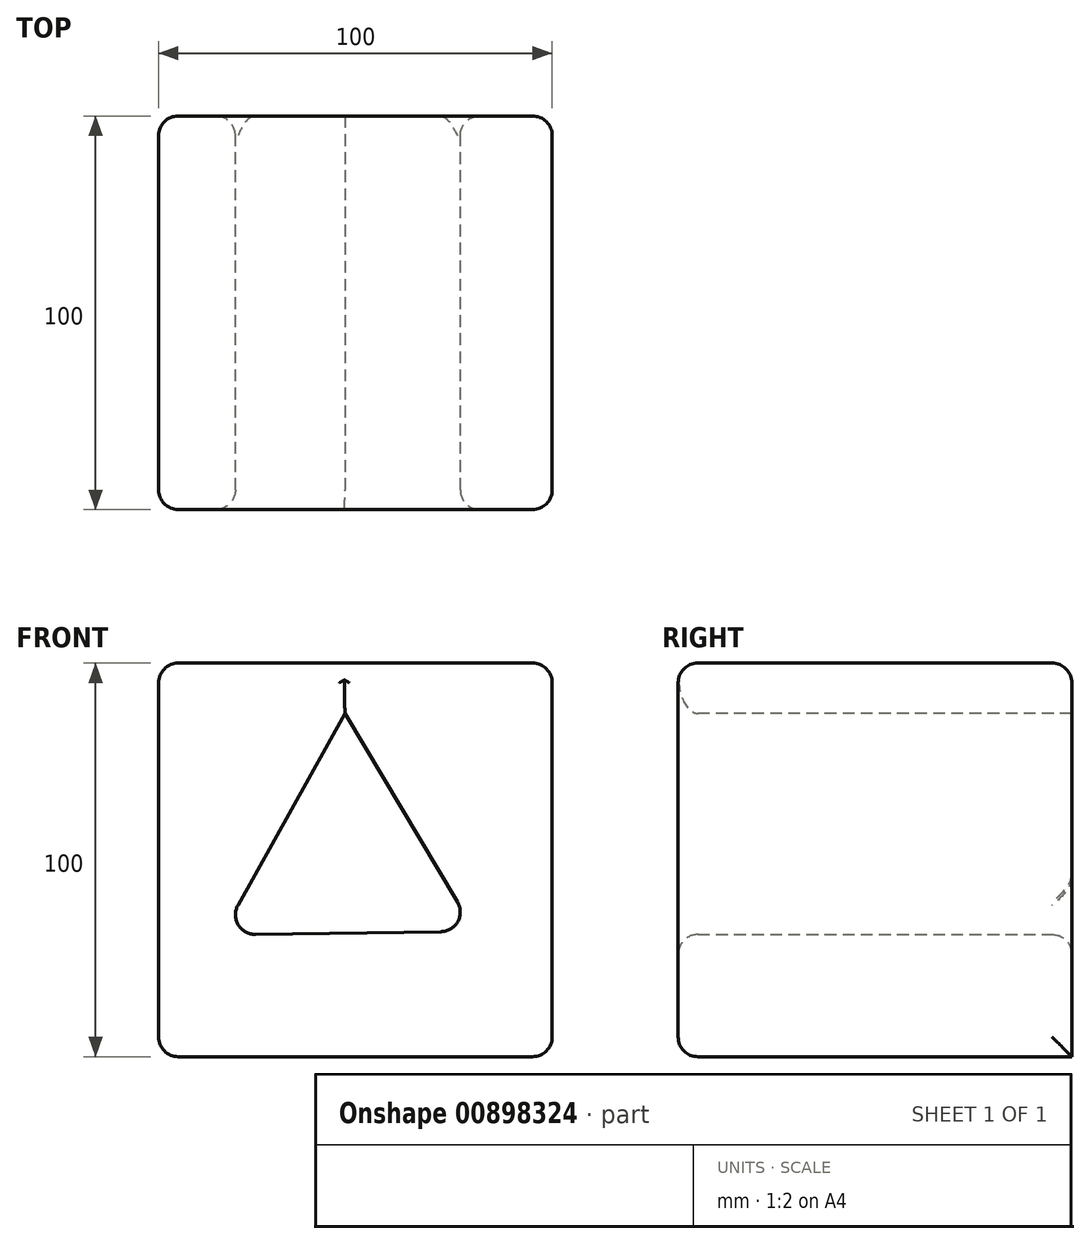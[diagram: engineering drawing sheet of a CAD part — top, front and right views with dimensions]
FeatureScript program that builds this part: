
annotation { "Feature Type Name" : "Feature", "Feature Type Description" : "" }
export const myFeature = defineFeature(function(context is Context, id is Id, definition is map)
    precondition{}
    {
        {
            var Q0;
            Q0=qCreatedBy(makeId("Front.planeOp"),FACE);
            var sketch = newSketch(context, id + "F0", { "sketchPlane" : qUnion([Q0])});
            skLineSegment(sketch, "E0.bottom", {"start": v(50, 50) * mm, "end": v(-50, 50) * mm});
            skLineSegment(sketch, "E0.top", {"start": v(50, -50) * mm, "end": v(-50, -50) * mm});
            skLineSegment(sketch, "E0.left", {"start": v(50, 50) * mm, "end": v(50, -50) * mm});
            skLineSegment(sketch, "E0.right", {"start": v(-50, 50) * mm, "end": v(-50, -50) * mm});
            skPoint(sketch, "E0.middle", {"position": v(0, 0) * mm});
            skSolve(sketch);
        }
        {
            var Q0;
            Q0=makeQuery(id+"F0.imprint","IMPRINT",FACE,{"disambiguationData":[TD([[makeQuery(id+"F0.imprint","IMPRINT",EDGE,{"derivedFrom":sQuery(id+"F0.wireOp",EDGE,"E0.bottom")}),1.0]])]});
            extrude(context, id + "F1", {"entities" : qUnion([Q0]), "depth" : 100 * mm, "offsetDistance" : 25 * mm});
        }
        {
            var Q0;
            Q0=makeQuery(id+"F1.opExtrude","CAP_FACE",FACE,{"disambiguationData":[OSD([sQuery(id+"F0.wireOp",EDGE,"E0.bottom"),sQuery(id+"F0.wireOp",EDGE,"E0.top"),sQuery(id+"F0.wireOp",EDGE,"E0.left"),sQuery(id+"F0.wireOp",EDGE,"E0.right")])],"isStart":false});
            var sketch = newSketch(context, id + "F2", { "sketchPlane" : qUnion([Q0])});
            skCircle(sketch, "E1.cCircle", {"center": v(-2.12, 0) * mm, "radius": 37.21 * mm, "construction": true});
            skLineSegment(sketch, "E1.0", {"start": v(30.38, -18.13) * mm, "end": v(-34.07, -19.08) * mm});
            skLineSegment(sketch, "E1.1", {"start": v(-34.07, -19.08) * mm, "end": v(-2.68, 37.2) * mm});
            skLineSegment(sketch, "E1.2", {"start": v(-2.68, 37.2) * mm, "end": v(30.38, -18.13) * mm});
            skSolve(sketch);
        }
        {
            var Q0;
            Q0=makeQuery(id+"F2.imprint","IMPRINT",FACE,{"disambiguationData":[TD([[makeQuery(id+"F2.imprint","IMPRINT",EDGE,{"derivedFrom":sQuery(id+"F2.wireOp",EDGE,"E1.0")}),-1.0]])]});
            extrude(context, id + "F3", {"entities" : qUnion([Q0]), "operationType" : NewBodyOperationType.REMOVE, "oppositeDirection" : true, "depth" : 447.2 * mm, "offsetDistance" : 25 * mm});
        }
        {
            var Q0;
            Q0=makeQuery(id+"F1.opExtrude","SWEPT_FACE",FACE,{"disambiguationData":[OSD([sQuery(id+"F0.wireOp",EDGE,"E0.left")])]});
            var Q1;
            Q1=makeQuery(id+"F1.opExtrude","CAP_FACE",FACE,{"disambiguationData":[OSD([sQuery(id+"F0.wireOp",EDGE,"E0.bottom"),sQuery(id+"F0.wireOp",EDGE,"E0.top"),sQuery(id+"F0.wireOp",EDGE,"E0.left"),sQuery(id+"F0.wireOp",EDGE,"E0.right")])],"isStart":false});
            var Q2;
            Q2=makeQuery(id+"F1.opExtrude","SWEPT_FACE",FACE,{"disambiguationData":[OSD([sQuery(id+"F0.wireOp",EDGE,"E0.bottom")])]});
            var Q3;
            Q3=makeQuery(id+"F3.boolean.opBoolean","COPY",FACE,{"derivedFrom":makeQuery(id+"F3.opExtrude","SWEPT_FACE",FACE,{"disambiguationData":[OSD([sQuery(id+"F2.wireOp",EDGE,"E1.0")])]})});
            fillet(context, id + "F4", {"entities" : qUnion([Q0, Q1, Q2, Q3]), "radius" : 5 * mm, "tangentPropagation" : true, "allowEdgeOverflow" : false});
        }
        {
            var Q0;
            Q0=makeQuery(id+"F1.opExtrude","SWEPT_FACE",FACE,{"disambiguationData":[OSD([sQuery(id+"F0.wireOp",EDGE,"E0.right")])]});
            fillet(context, id + "F5", {"entities" : qUnion([Q0]), "radius" : 5 * mm, "tangentPropagation" : true, "allowEdgeOverflow" : false});
        }
    });
